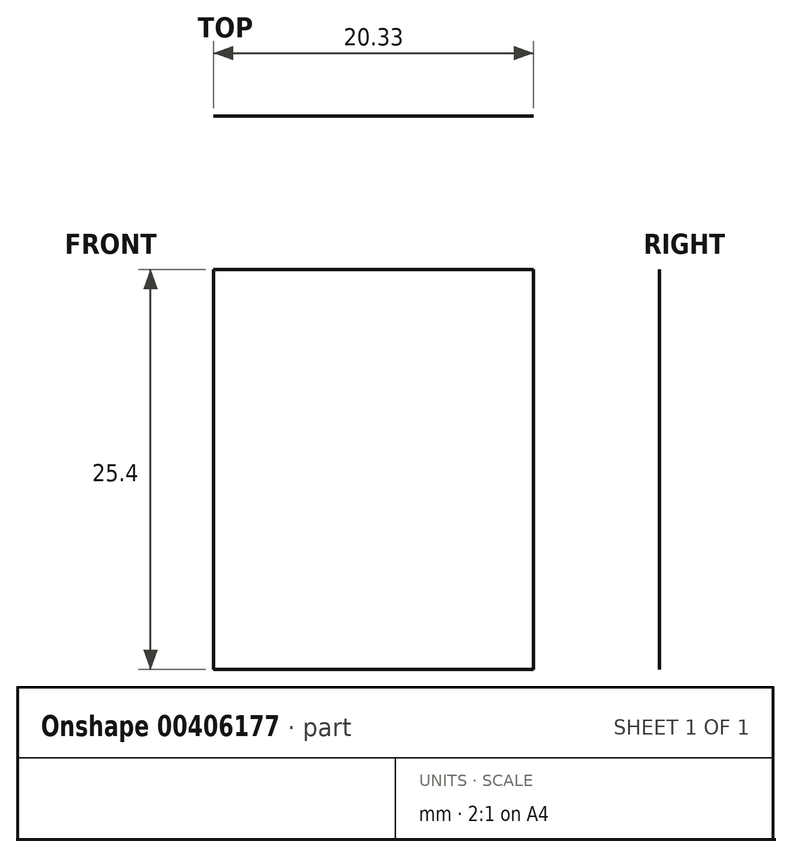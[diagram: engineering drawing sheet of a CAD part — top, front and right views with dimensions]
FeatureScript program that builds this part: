
annotation { "Feature Type Name" : "Feature", "Feature Type Description" : "" }
export const myFeature = defineFeature(function(context is Context, id is Id, definition is map)
    precondition{}
    {
        {
            var Q0;
            Q0=qCreatedBy(makeId("Top.planeOp"),FACE);
            var sketch = newSketch(context, id + "F0", { "sketchPlane" : qUnion([Q0])});
            skLineSegment(sketch, "E0.bottom", {"start": v(-20.33, 65.42) * mm, "end": v(0, 65.42) * mm});
            skLineSegment(sketch, "E0.top", {"start": v(-20.33, -64.53) * mm, "end": v(0, -64.53) * mm});
            skLineSegment(sketch, "E0.left", {"start": v(-20.33, 65.42) * mm, "end": v(-20.33, -64.53) * mm});
            skLineSegment(sketch, "E0.right", {"start": v(0, 65.42) * mm, "end": v(0, -64.53) * mm});
            skSolve(sketch);
        }
        {
            var Q0;
            Q0=sQuery(id+"F0.wireOp",EDGE,"E0.bottom");
            extrude(context, id + "F1", {"bodyType" : ToolBodyType.SURFACE, "surfaceEntities" : qUnion([Q0]), "depth" : 25.4 * mm});
        }
    });
